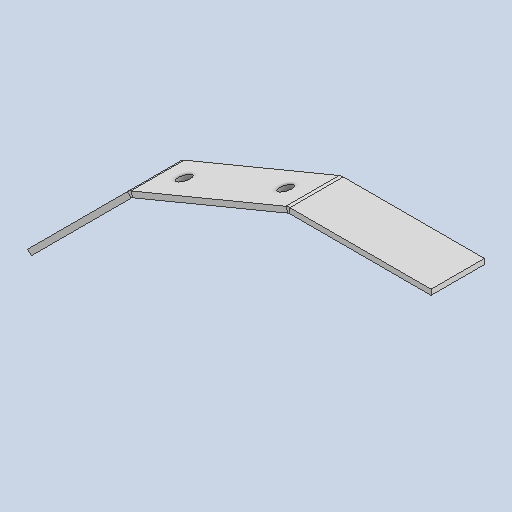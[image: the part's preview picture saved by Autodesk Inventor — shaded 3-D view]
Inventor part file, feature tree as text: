
AUTODESK INVENTOR PART (.ipt)
format: ipt  version: 2025 (Build 290162010, 162A)  size: 131,584 bytes
history: native  units: mm
features: sheet_metal_op x3, sketch x2, extrude x1, other x1
ambient origin geometry x8: Origin, YZ Plane, XZ Plane, XY Plane, X Axis, Y Axis, Z Axis, Center Point
bodies: Solid1 (feature_tree)
feature tree (7):
  sheet_metal_op  "Contour Flange1"
  extrude  "Extrusion1"  Depth=5.0mm
  sketch  "Sketch2"  dims[d0=513.0mm d1=260.0mm d2=635.0mm d6=5.0mm]
  other  "Plate1"
  sheet_metal_op  "Bend1"
  sheet_metal_op  "Corner1"
  sketch  "Sketch3"  dims[d10=5.0mm d14=5.0mm d15=16.0mm d16=8.0mm d17=8.0mm d18=4.0mm d19=16.0mm d20=8.0mm d21=80.0mm d22=8.0mm d23=8.0mm d24=32.0mm d25=8.0mm d26=8.0mm d27=20.0mm d28=82.5mm d30=0.0mm d31=0.0mm]
